# Revit family: NBS_DudleyIndustriesLimited_PprTwlDpnsrs_ClassicBehindTheMirrorRangePullDownPaperTowelDispenser
name_source: partatom
category: Specialty Equipment
units: mm (PartAtom-declared; Revit-internal decimal feet)

## family parameters
Cut with Voids When Loaded = No
Host = Face
Part Type = Normal
Room Calculation Point = No
Round Connector Dimension = Use Diameter
Shared = No

## types (1)
- ClassicBehindTheMirrorPullDownPaperTowelDispenser
    AssetType = Fixed
    BIMObjectName = NBS_DudleyIndustriesLimited_PaperTowelDispensers_ClassicBehindTheMirrorPullDownPaperTowelDispenser
    Category = Pr_40_70_22_62:Paper towel dispensers
    ClearanceZoneMaterial = NBS_ClearanceZone
    Color = Silver
    CountryOfMaterialOrigin = United Kingdom
    CountryOfProductManufacture = United Kingdom
    Default Elevation = 0 mm  [stored 0 ft]
    Description = Paper Towel dispenser with large capacity, for discrete installation behind a mirror or cabinet. Conveniently pulls down below the unit for ease of refilling
    DispenserMaterial = NBS_DudleyIndustriesLimited_StainlessSteel_Brushed
    DurationUnit = year
    Features = Holds 2 standard packs of interleaved paper towels, maximum size of paper towel 270mm x 120mm when folded, base securely locks into position to secure the consumables, co-ordinating Soaps Dispensers also available
    Finish = Other
    Fixings = Four base panel fixings
    Form = Wall-mounted
    IfcExportAs = IfcFurnitureType
    IfcExportType = USERDEFINED
    ManufacturerName = Dudley Industries Limited
    ManufacturerURL = www.dudleyindustries.com
    Material = Stainless steel
    MaterialsBody = Stainless Steel
    MaterialsFinishAndColour = Silver
    ModelNumber = 92070SS
    ModelReference = Classic Behind the Mirror Pull Down Paper Towel Dispenser
    NBSInstanceId = 27ef8de9-38a0-4f12-a059-24896da42627
    NBSObjectId = bf8eba6f-f173-4fb2-960d-bf041898e9dc
    NBSVariantId = 00000000-0000-0000-0000-000000000000
    Name = PaperTowelDispensers_ClassicBehindTheMirrorPullDownPaperTowelDispenser_DudleyIndustriesLimited
    NominalHeight = 353 mm  [stored 1.15814 ft]
    NominalLength = 170 mm  [stored 0.557743 ft]
    NominalWidth = 353 mm  [stored 1.15814 ft]
    Operation = Pull-down
    ProductInformation = https://source.thenbs.com
    Shape = Rectangle
    Size = 353 x 353 x 170 mm
    TowelsTowelType = Folded
    TowelsWidth = 270 mm
    Uniclass2015Code = Pr_40_70_22_62
    Uniclass2015Title = Paper towel dispensers
    Uniclass2015Version = Products v1.30
    Version = 2
    WarrantyDescription = Ten year
    WarrantyDurationUnit = year

note: [stored X ft] marks values corroborated as IEEE doubles in the binary element streams (Revit-internal decimal feet)

## geometry (parser evidence)
native form markers: Sweep x2
no freeform markers — native parametric forms only
